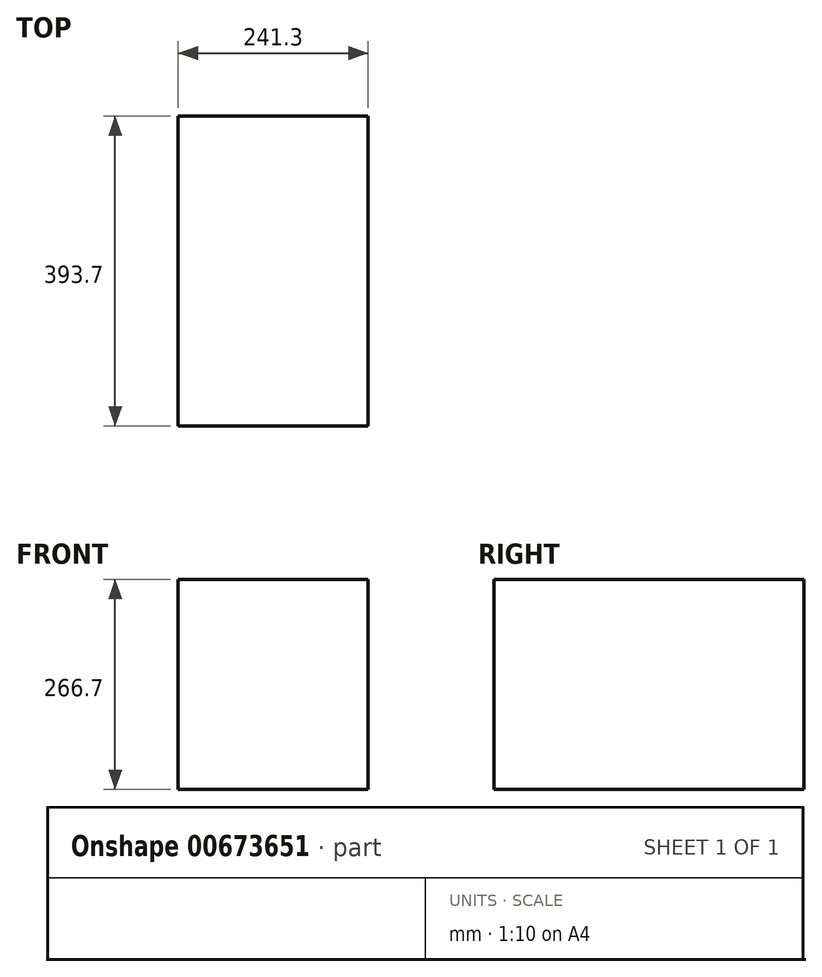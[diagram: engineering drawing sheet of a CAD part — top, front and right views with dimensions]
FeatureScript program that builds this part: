
annotation { "Feature Type Name" : "Feature", "Feature Type Description" : "" }
export const myFeature = defineFeature(function(context is Context, id is Id, definition is map)
    precondition{}
    {
        {
            var Q0;
            Q0=qCreatedBy(makeId("Top.planeOp"),FACE);
            var sketch = newSketch(context, id + "F0", { "sketchPlane" : qUnion([Q0])});
            skLineSegment(sketch, "E0.bottom", {"start": v(-120.65, 196.85) * mm, "end": v(120.65, 196.85) * mm});
            skLineSegment(sketch, "E0.top", {"start": v(-120.65, -196.85) * mm, "end": v(120.65, -196.85) * mm});
            skLineSegment(sketch, "E0.left", {"start": v(-120.65, 196.85) * mm, "end": v(-120.65, -196.85) * mm});
            skLineSegment(sketch, "E0.right", {"start": v(120.65, 196.85) * mm, "end": v(120.65, -196.85) * mm});
            skPoint(sketch, "E0.middle", {"position": v(0, 0) * mm});
            skSolve(sketch);
        }
        {
            var Q0;
            Q0 = qSketchRegion(id + "F0", true);
            extrude(context, id + "F1", {"entities" : qUnion([Q0]), "depth" : 266.7 * mm, "offsetDistance" : 25.4 * mm});
        }
    });
